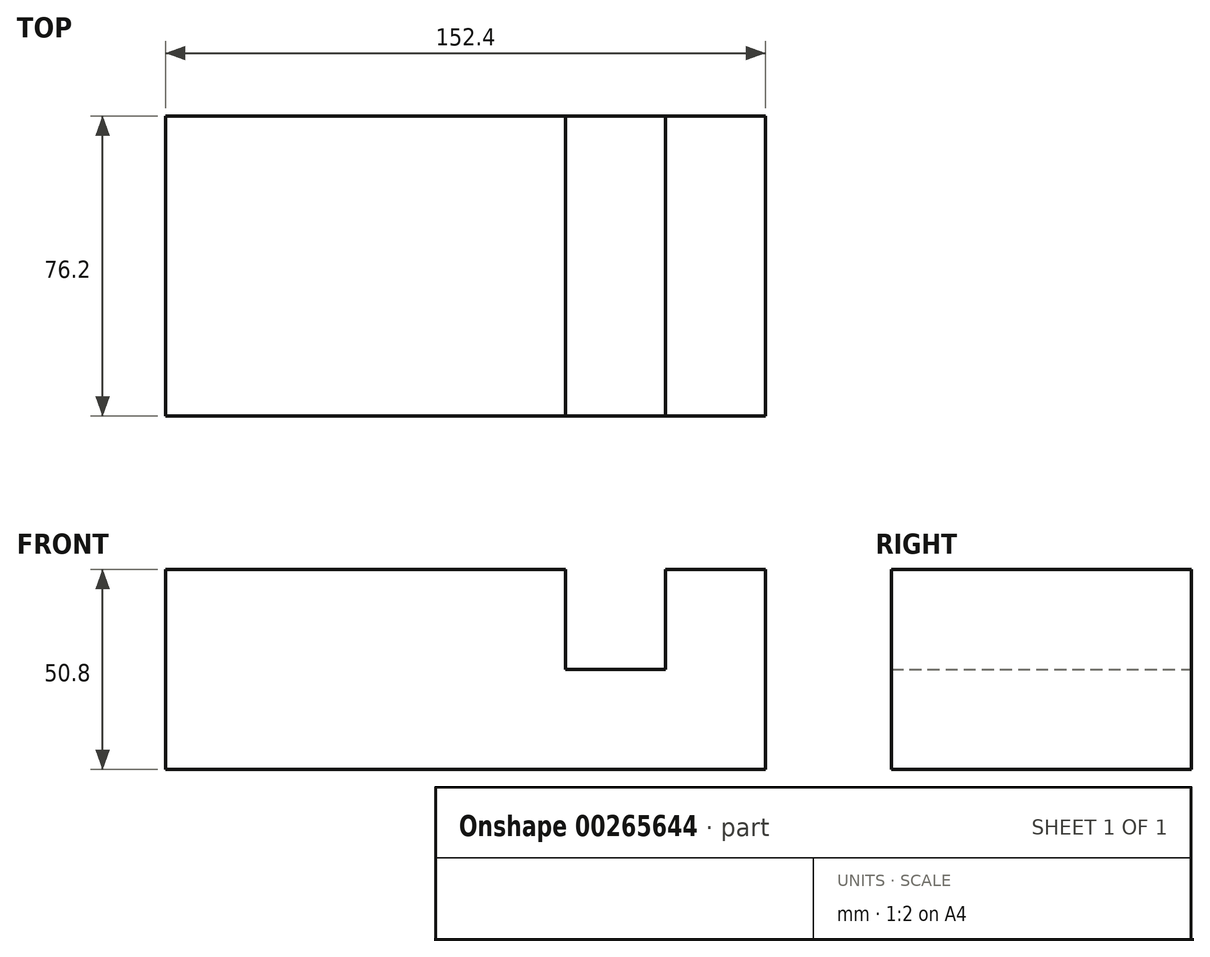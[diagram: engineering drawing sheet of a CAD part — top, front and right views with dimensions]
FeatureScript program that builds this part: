
annotation { "Feature Type Name" : "Feature", "Feature Type Description" : "" }
export const myFeature = defineFeature(function(context is Context, id is Id, definition is map)
    precondition{}
    {
        {
            var Q0;
            Q0=qCreatedBy(makeId("Front.planeOp"),FACE);
            var sketch = newSketch(context, id + "F0", { "sketchPlane" : qUnion([Q0])});
            skLineSegment(sketch, "E0", {"start": v(0, 50.8) * mm, "end": v(0, 0) * mm});
            skLineSegment(sketch, "E1", {"start": v(0, 0) * mm, "end": v(152.4, 0) * mm});
            skLineSegment(sketch, "E2", {"start": v(0, 50.8) * mm, "end": v(101.6, 50.8) * mm});
            skLineSegment(sketch, "E3", {"start": v(101.6, 50.8) * mm, "end": v(101.6, 25.4) * mm});
            skLineSegment(sketch, "E4", {"start": v(101.6, 25.4) * mm, "end": v(127, 25.4) * mm});
            skLineSegment(sketch, "E5", {"start": v(152.4, 0) * mm, "end": v(152.4, 50.8) * mm});
            skLineSegment(sketch, "E6", {"start": v(127, 25.4) * mm, "end": v(127, 50.8) * mm});
            skLineSegment(sketch, "E7", {"start": v(127, 50.8) * mm, "end": v(152.4, 50.8) * mm});
            skSolve(sketch);
        }
        {
            var Q0;
            Q0 = qSketchRegion(id + "F0", true);
            extrude(context, id + "F1", {"entities" : qUnion([Q0]), "depth" : 25.4 * mm});
        }
        {
            var Q0;
            Q0 = qSketchRegion(id + "F0", true);
            extrude(context, id + "F2", {"entities" : qUnion([Q0]), "operationType" : NewBodyOperationType.ADD, "depth" : 76.2 * mm});
        }
    });
